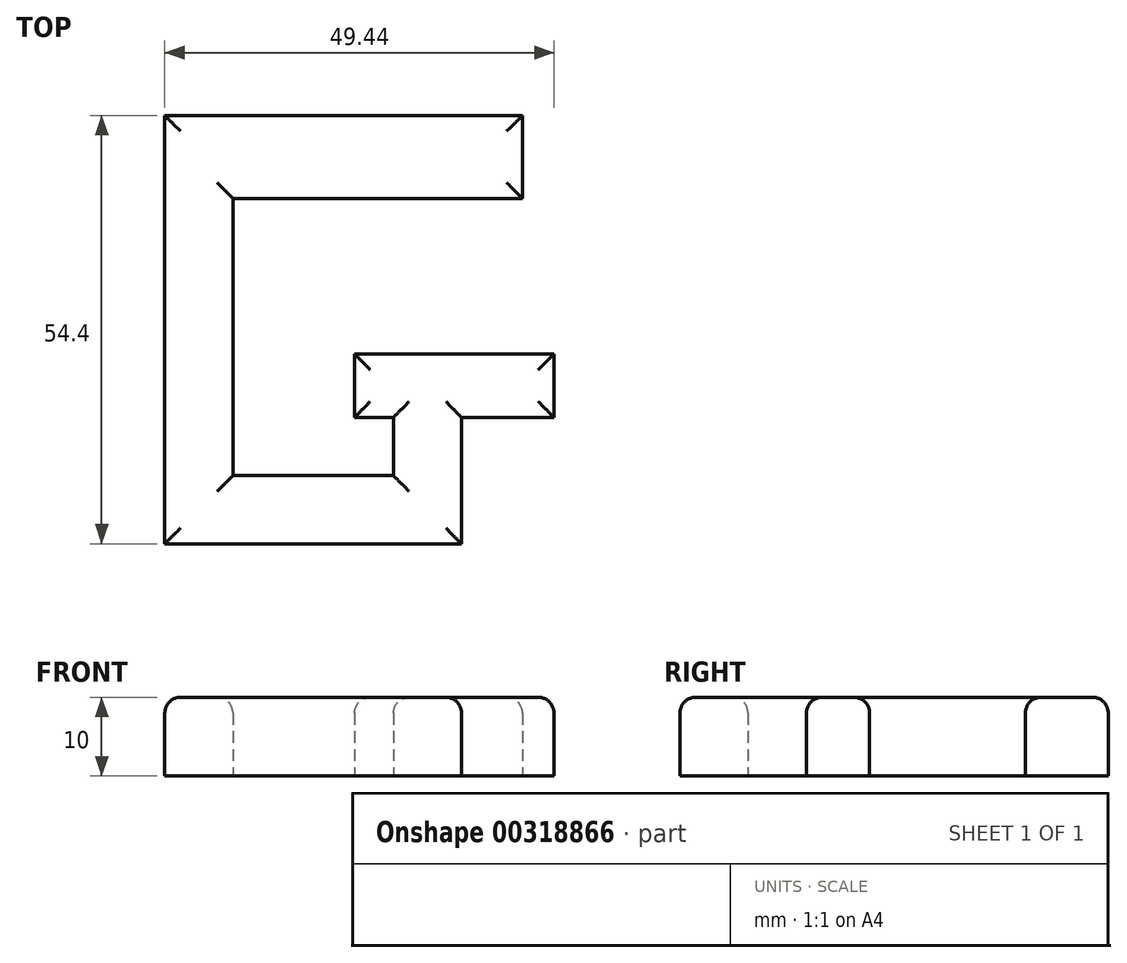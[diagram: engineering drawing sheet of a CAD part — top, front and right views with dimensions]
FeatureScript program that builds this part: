
annotation { "Feature Type Name" : "Feature", "Feature Type Description" : "" }
export const myFeature = defineFeature(function(context is Context, id is Id, definition is map)
    precondition{}
    {
        {
            var Q0;
            Q0=qCreatedBy(makeId("Top.planeOp"),FACE);
            var sketch = newSketch(context, id + "F0", { "sketchPlane" : qUnion([Q0])});
            skLineSegment(sketch, "E0", {"start": v(0, 0) * mm, "end": v(-36.78, 0) * mm});
            skLineSegment(sketch, "E1", {"start": v(-36.78, 0) * mm, "end": v(-45.43, 0) * mm});
            skLineSegment(sketch, "E2", {"start": v(-45.43, 0) * mm, "end": v(-45.43, -54.4) * mm});
            skLineSegment(sketch, "E3", {"start": v(-45.43, -54.4) * mm, "end": v(-7.73, -54.4) * mm});
            skLineSegment(sketch, "E4", {"start": v(-7.73, -54.4) * mm, "end": v(-7.73, -38.34) * mm});
            skLineSegment(sketch, "E5", {"start": v(-7.73, -38.34) * mm, "end": v(4, -38.34) * mm});
            skLineSegment(sketch, "E6", {"start": v(4, -38.34) * mm, "end": v(4, -30.3) * mm});
            skLineSegment(sketch, "E7", {"start": v(4, -30.3) * mm, "end": v(-21.33, -30.3) * mm});
            skLineSegment(sketch, "E8", {"start": v(-21.33, -30.3) * mm, "end": v(-21.33, -38.34) * mm});
            skLineSegment(sketch, "E9", {"start": v(-21.33, -38.34) * mm, "end": v(-16.38, -38.34) * mm});
            skLineSegment(sketch, "E10", {"start": v(-16.38, -38.34) * mm, "end": v(-16.38, -45.75) * mm});
            skLineSegment(sketch, "E11", {"start": v(-16.38, -45.75) * mm, "end": v(-36.78, -45.75) * mm});
            skLineSegment(sketch, "E12", {"start": v(-36.78, -45.75) * mm, "end": v(-36.78, -10.53) * mm});
            skLineSegment(sketch, "E13", {"start": v(-36.78, -10.53) * mm, "end": v(-8.35, -10.53) * mm});
            skLineSegment(sketch, "E14", {"start": v(-8.35, -10.53) * mm, "end": v(0, -10.53) * mm});
            skLineSegment(sketch, "E15", {"start": v(0, -10.53) * mm, "end": v(0, 0) * mm});
            skSolve(sketch);
        }
        {
            var Q0;
            Q0 = qSketchRegion(id + "F0", true);
            extrude(context, id + "F1", {"entities" : qUnion([Q0]), "depth" : 10 * mm});
        }
        {
            var Q0;
            Q0=makeQuery(id+"F1.opExtrude","CAP_FACE",FACE,{"disambiguationData":[OSD([sQuery(id+"F0.wireOp",EDGE,"E0"),sQuery(id+"F0.wireOp",EDGE,"E1"),sQuery(id+"F0.wireOp",EDGE,"E2"),sQuery(id+"F0.wireOp",EDGE,"E3"),sQuery(id+"F0.wireOp",EDGE,"E4"),sQuery(id+"F0.wireOp",EDGE,"E5"),sQuery(id+"F0.wireOp",EDGE,"E6"),sQuery(id+"F0.wireOp",EDGE,"E7"),sQuery(id+"F0.wireOp",EDGE,"E8"),sQuery(id+"F0.wireOp",EDGE,"E9"),sQuery(id+"F0.wireOp",EDGE,"E10"),sQuery(id+"F0.wireOp",EDGE,"E11"),sQuery(id+"F0.wireOp",EDGE,"E12"),sQuery(id+"F0.wireOp",EDGE,"E13"),sQuery(id+"F0.wireOp",EDGE,"E14"),sQuery(id+"F0.wireOp",EDGE,"E15")])],"isStart":false});
            fillet(context, id + "F2", {"entities" : qUnion([Q0]), "radius" : 2 * mm, "tangentPropagation" : true, "allowEdgeOverflow" : false});
        }
    });
